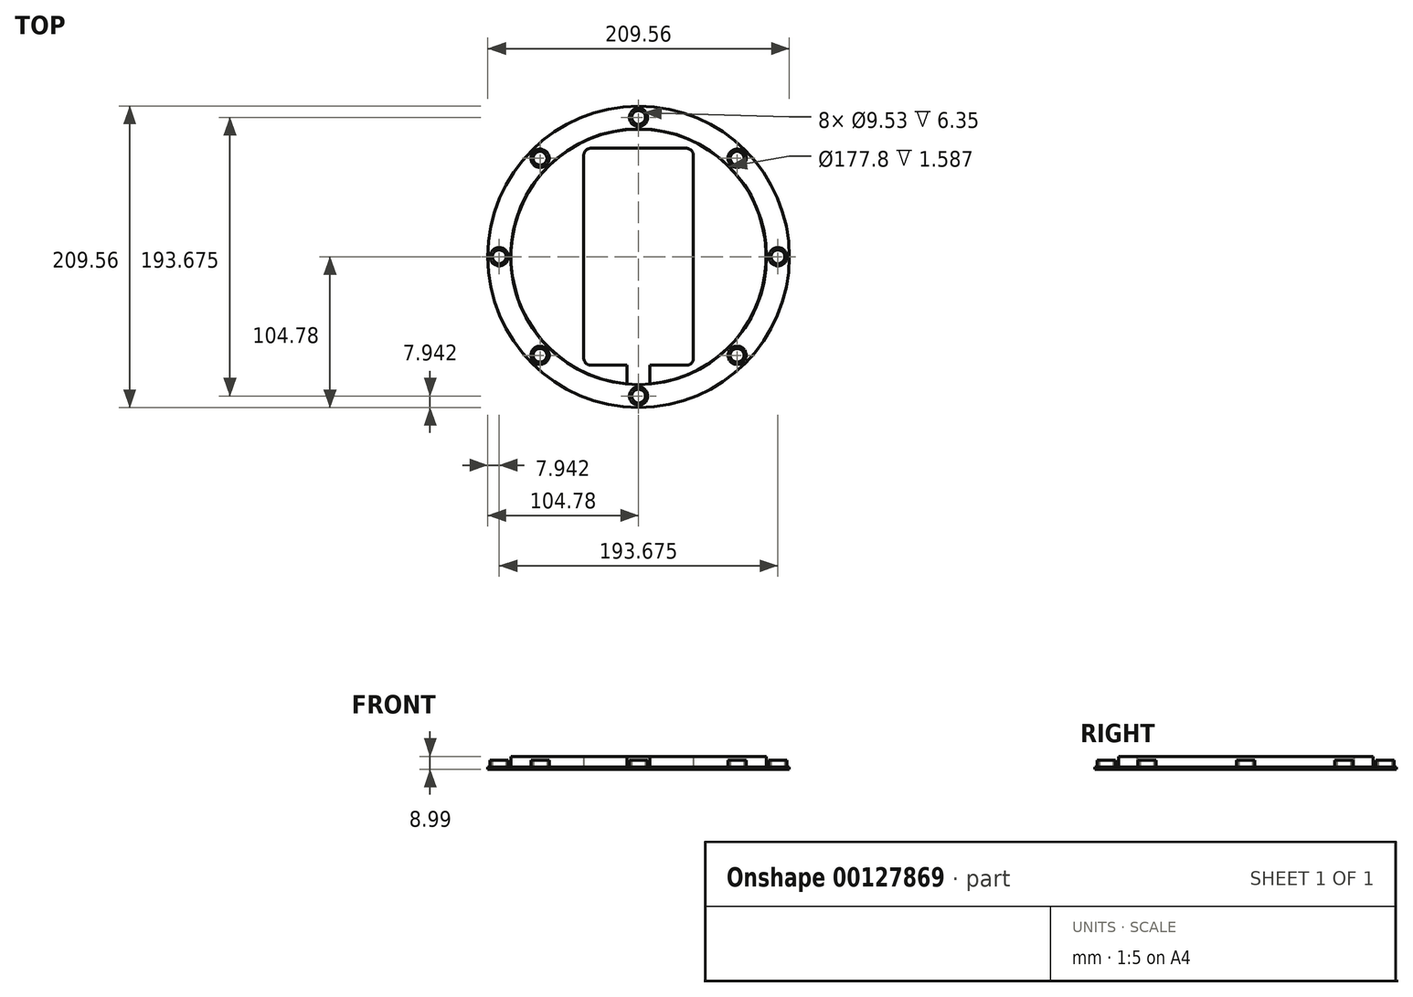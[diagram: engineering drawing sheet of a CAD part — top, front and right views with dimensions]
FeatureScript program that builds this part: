
annotation { "Feature Type Name" : "Feature", "Feature Type Description" : "" }
export const myFeature = defineFeature(function(context is Context, id is Id, definition is map)
    precondition{}
    {
        {
            var Q0;
            Q0=qCreatedBy(makeId("Top.planeOp"),FACE);
            var sketch = newSketch(context, id + "F0", { "sketchPlane" : qUnion([Q0])});
            skCircle(sketch, "E0", {"center": v(0, 0) * mm, "radius": 88.65 * mm});
            skLineSegment(sketch, "E1.bottom", {"start": v(33.1, 75.4) * mm, "end": v(-33.1, 75.4) * mm});
            skLineSegment(sketch, "E1.top", {"start": v(33.1, -75.4) * mm, "end": v(-33.1, -75.4) * mm});
            skLineSegment(sketch, "E1.left", {"start": v(38.1, 70.4) * mm, "end": v(38.1, -70.4) * mm});
            skLineSegment(sketch, "E1.right", {"start": v(-38.1, 70.4) * mm, "end": v(-38.1, -70.4) * mm});
            skPoint(sketch, "E2.visualSharp", {"position": v(-38.1, 75.4) * mm});
            skArc(sketch, "E2.filletArc", {"start": v(-33.1, 75.4) * mm, "mid": v(-36.64, 73.94) * mm, "end": v(-38.1, 70.4) * mm});
            skPoint(sketch, "E3.visualSharp", {"position": v(38.1, 75.4) * mm});
            skArc(sketch, "E3.filletArc", {"start": v(38.1, 70.4) * mm, "mid": v(36.64, 73.94) * mm, "end": v(33.1, 75.4) * mm});
            skPoint(sketch, "E4.visualSharp", {"position": v(38.1, -75.4) * mm});
            skArc(sketch, "E4.filletArc", {"start": v(33.1, -75.4) * mm, "mid": v(36.64, -73.94) * mm, "end": v(38.1, -70.4) * mm});
            skPoint(sketch, "E5.visualSharp", {"position": v(-38.1, -75.4) * mm});
            skArc(sketch, "E5.filletArc", {"start": v(-38.1, -70.4) * mm, "mid": v(-36.64, -73.94) * mm, "end": v(-33.1, -75.4) * mm});
            skLineSegment(sketch, "E6.bottom", {"start": v(7.94, -99.5) * mm, "end": v(-7.94, -99.5) * mm});
            skLineSegment(sketch, "E6.top", {"start": v(7.94, -69.5) * mm, "end": v(-7.94, -69.5) * mm});
            skLineSegment(sketch, "E6.left", {"start": v(7.94, -99.5) * mm, "end": v(7.94, -69.5) * mm});
            skLineSegment(sketch, "E6.right", {"start": v(-7.94, -99.5) * mm, "end": v(-7.94, -69.5) * mm});
            skPoint(sketch, "E6.middle", {"position": v(0, -84.5) * mm});
            skSolve(sketch);
        }
        {
            var Q0;
            Q0=makeQuery(id+"F0.imprint","IMPRINT",FACE,{"disambiguationData":[TD([[makeQuery(id+"F0.imprint","IMPRINT",EDGE,{"derivedFrom":sQuery(id+"F0.wireOp",EDGE,"E1.bottom")}),-1.0]])]});
            extrude(context, id + "F1", {"entities" : qUnion([Q0]), "depth" : 9 * mm});
        }
        {
            var Q0;
            Q0=qCreatedBy(makeId("Top.planeOp"),FACE);
            var sketch = newSketch(context, id + "F2", { "sketchPlane" : qUnion([Q0])});
            skCircle(sketch, "E7", {"center": v(0, 0) * mm, "radius": 88.9 * mm});
            skCircle(sketch, "E8", {"center": v(0, 0) * mm, "radius": 104.78 * mm});
            skCircle(sketch, "E9", {"center": v(96.84, 0) * mm, "radius": 4.76 * mm});
            skCircle(sketch, "E10.1.0", {"center": v(68.47, 68.47) * mm, "radius": 4.76 * mm});
            skCircle(sketch, "E10.2.0", {"center": v(0, 96.84) * mm, "radius": 4.76 * mm});
            skCircle(sketch, "E10.3.0", {"center": v(-68.47, 68.47) * mm, "radius": 4.76 * mm});
            skCircle(sketch, "E10.4.0", {"center": v(-96.84, 0) * mm, "radius": 4.76 * mm});
            skCircle(sketch, "E10.5.0", {"center": v(-68.47, -68.47) * mm, "radius": 4.76 * mm});
            skCircle(sketch, "E10.6.0", {"center": v(0, -96.84) * mm, "radius": 4.76 * mm});
            skCircle(sketch, "E10.7.0", {"center": v(68.47, -68.47) * mm, "radius": 4.76 * mm});
            skSolve(sketch);
        }
        {
            var Q0;
            Q0=makeQuery(id+"F2.imprint","IMPRINT",FACE,{"disambiguationData":[TD([[makeQuery(id+"F2.imprint","IMPRINT",EDGE,{"derivedFrom":sQuery(id+"F2.wireOp",EDGE,"E7")}),-1.0]])]});
            extrude(context, id + "F3", {"entities" : qUnion([Q0]), "depth" : 1.59 * mm});
        }
        {
            var Q0;
            Q0=makeQuery(id+"F3.opExtrude","CAP_FACE",FACE,{"disambiguationData":[OSD([sQuery(id+"F2.wireOp",EDGE,"E7"),sQuery(id+"F2.wireOp",EDGE,"E8"),sQuery(id+"F2.wireOp",EDGE,"E9"),sQuery(id+"F2.wireOp",EDGE,"E10.1.0"),sQuery(id+"F2.wireOp",EDGE,"E10.2.0"),sQuery(id+"F2.wireOp",EDGE,"E10.3.0"),sQuery(id+"F2.wireOp",EDGE,"E10.4.0"),sQuery(id+"F2.wireOp",EDGE,"E10.5.0"),sQuery(id+"F2.wireOp",EDGE,"E10.6.0"),sQuery(id+"F2.wireOp",EDGE,"E10.7.0")])],"isStart":false});
            var sketch = newSketch(context, id + "F4", { "sketchPlane" : qUnion([Q0])});
            skCircle(sketch, "E11", {"center": v(96.84, 0) * mm, "radius": 4.76 * mm});
            skCircle(sketch, "E12", {"center": v(96.84, 0) * mm, "radius": 6.35 * mm});
            skCircle(sketch, "E13.1.0", {"center": v(68.47, 68.47) * mm, "radius": 4.76 * mm});
            skCircle(sketch, "E13.1.1", {"center": v(68.47, 68.47) * mm, "radius": 6.35 * mm});
            skCircle(sketch, "E13.2.0", {"center": v(0, 96.84) * mm, "radius": 4.76 * mm});
            skCircle(sketch, "E13.2.1", {"center": v(0, 96.84) * mm, "radius": 6.35 * mm});
            skCircle(sketch, "E13.3.0", {"center": v(-68.47, 68.47) * mm, "radius": 4.76 * mm});
            skCircle(sketch, "E13.3.1", {"center": v(-68.47, 68.47) * mm, "radius": 6.35 * mm});
            skCircle(sketch, "E13.4.0", {"center": v(-96.84, 0) * mm, "radius": 4.76 * mm});
            skCircle(sketch, "E13.4.1", {"center": v(-96.84, 0) * mm, "radius": 6.35 * mm});
            skCircle(sketch, "E13.5.0", {"center": v(-68.47, -68.47) * mm, "radius": 4.76 * mm});
            skCircle(sketch, "E13.5.1", {"center": v(-68.47, -68.47) * mm, "radius": 6.35 * mm});
            skCircle(sketch, "E13.6.0", {"center": v(0, -96.84) * mm, "radius": 4.76 * mm});
            skCircle(sketch, "E13.6.1", {"center": v(0, -96.84) * mm, "radius": 6.35 * mm});
            skCircle(sketch, "E13.7.0", {"center": v(68.47, -68.47) * mm, "radius": 4.76 * mm});
            skCircle(sketch, "E13.7.1", {"center": v(68.47, -68.47) * mm, "radius": 6.35 * mm});
            skPoint(sketch, "E13.center", {"position": v(0, 0) * mm});
            skSolve(sketch);
        }
        {
            var Q0;
            Q0 = qSketchRegion(id + "F4", true);
            extrude(context, id + "F5", {"entities" : qUnion([Q0]), "operationType" : NewBodyOperationType.ADD, "depth" : 4.76 * mm});
        }
        {
            var Q0;
            Q0=qCreatedBy(makeId("Front.planeOp"),FACE);
            var sketch = newSketch(context, id + "F6", { "sketchPlane" : qUnion([Q0])});
            skArc(sketch, "E14", {"start": v(96.7, 9.47) * mm, "mid": v(101.47, 4.71) * mm, "end": v(96.7, -0.05) * mm});
            skLineSegment(sketch, "E15", {"start": v(96.7, 10.3) * mm, "end": v(96.7, 62.68) * mm});
            skSolve(sketch);
        }
        {
            var Q0;
            Q0=sQuery(id+"F6.wireOp",EDGE,"E14");
            var Q1;
            Q1=sQuery(id+"F6.wireOp",EDGE,"E15");
            revolve(context, id + "F7", {"bodyType" : ToolBodyType.SURFACE, "surfaceEntities" : qUnion([Q0]), "axis" : qUnion([Q1]), "revolveType" : RevolveType.FULL});
        }
        {
            var Q0;
            Q0=qCreatedBy(makeId("Front.planeOp"),FACE);
            var sketch = newSketch(context, id + "F8", { "sketchPlane" : qUnion([Q0])});
            skLineSegment(sketch, "E16", {"start": v(0, 0) * mm, "end": v(0, 64.63) * mm});
            skSolve(sketch);
        }
        {
            var Q0;
            Q0=makeQuery(id+"F7.opRevolve","SWEPT_BODY",BODY,{"disambiguationData":[OSD([sQuery(id+"F6.wireOp",EDGE,"E14")])]});
            var Q1;
            Q1=sQuery(id+"F8.wireOp",EDGE,"E16");
            circularPattern(context, id + "F9", {"entities" : qUnion([Q0]), "axis" : qUnion([Q1]), "angle" : 45 * degree, "instanceCount" : 8});
        }
    });
